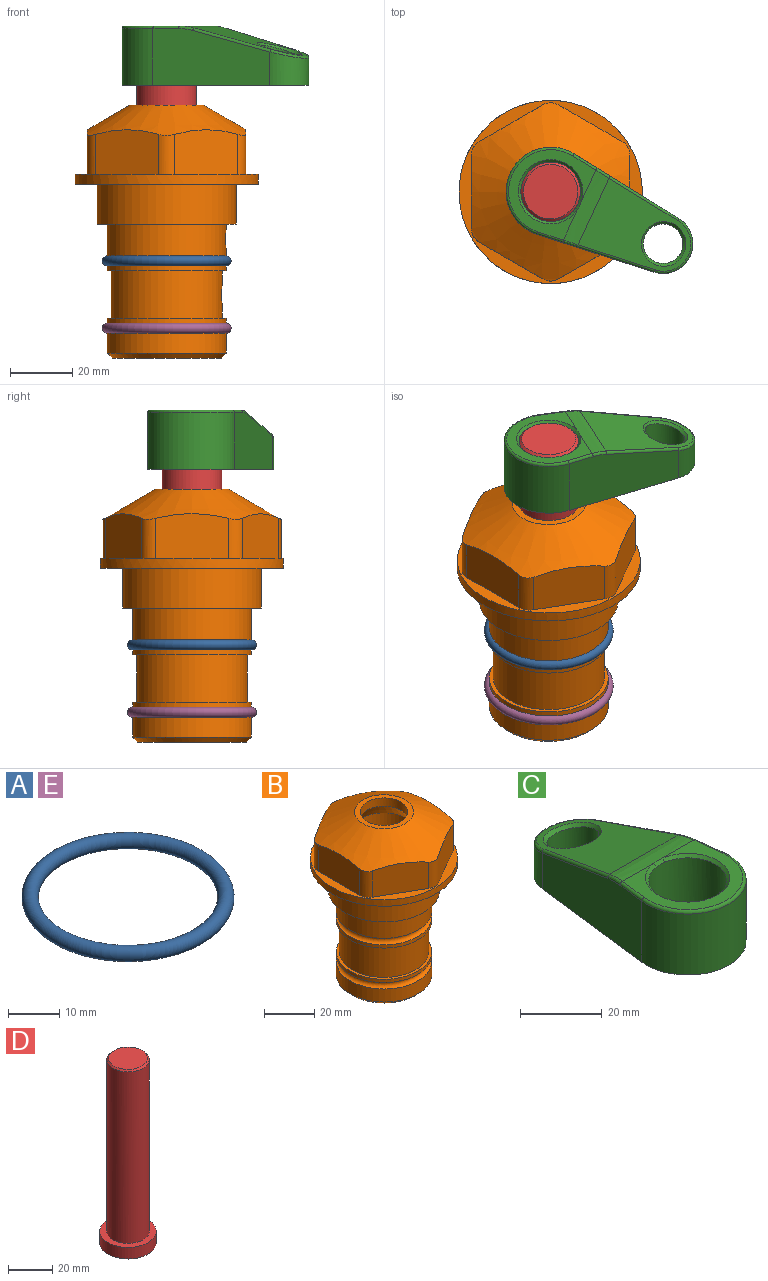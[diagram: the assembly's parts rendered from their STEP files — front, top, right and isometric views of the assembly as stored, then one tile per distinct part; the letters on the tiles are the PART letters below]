
ASSEMBLY  parts=5 mates=4
PART A: 1 faces, bbox 44.7x44.7x3.2 mm
  f0: torus R=19.05mm, axis (0,0,1), area 1193.9mm2
PART B: 36 faces, bbox 58.7x58.7x81 mm
  f0: cylinder r=17.78mm len=35.56mm, axis (0,0,1), area 1670.8mm2, adj f23,f24,f31
  f1: cylinder r=19.05mm len=38.1mm, axis (0,0,1), area 1191.9mm2, adj f26,f27,f30
  f2: plane 58.66x58.66mm, normal (0,0,-1), area 1150.6mm2, adj f3,f28
  f3: cylinder r=29.33mm len=58.66mm, axis (0,0,-1), area 585.1mm2, adj f2,f4
  f4: plane 58.66x58.66mm, normal (0,0,1), area 475.9mm2, adj f3,f5,f6,f7,f8,f9,f10,f11
  f5: plane 20.32x14.34mm, normal (-0.5,0.87,0), area 324.4mm2, adj f4,f15,f16,f17
  f6: plane 20.32x14.34mm, normal (0.5,0.87,0), area 324.4mm2, adj f4,f14,f15,f17
  f7: plane 23.48x14.34mm, normal (1,0,0), area 324.4mm2, adj f4,f13,f14,f17
  f8: plane 20.32x14.34mm, normal (0.5,-0.87,0), area 324.4mm2, adj f4,f12,f13,f17
  f9: plane 20.32x14.34mm, normal (-0.5,-0.87,0), area 324.4mm2, adj f4,f11,f12,f17
  f10: plane 23.48x14.34mm, normal (-1,0,0), area 324.4mm2, adj f4,f11,f16,f17
  f11: cylinder r=5.08mm len=12.85mm, axis (0,0,-1), area 67.2mm2, adj f4,f9,f10,f17
  f12: cylinder r=5.08mm len=12.85mm, axis (0,0,-1), area 67.2mm2, adj f4,f8,f9,f17
  f13: cylinder r=5.08mm len=12.85mm, axis (0,0,-1), area 67.2mm2, adj f4,f7,f8,f17
  f14: cylinder r=5.08mm len=12.85mm, axis (0,0,-1), area 67.2mm2, adj f4,f6,f7,f17
  f15: cylinder r=5.08mm len=12.85mm, axis (0,0,-1), area 67.2mm2, adj f4,f5,f6,f17
  f16: cylinder r=5.08mm len=12.85mm, axis (0,0,-1), area 67.2mm2, adj f4,f5,f10,f17
  f17: cone r=11.73mm half-angle=60deg, axis (0,0,-1), area 2071.8mm2, adj f5,f6,f7,f8,f9,f10,f11,f12
  f18: plane 23.46x23.46mm, normal (0,0,1), area 147.4mm2, adj f17,f35
  f19: plane 34.93x34.93mm, normal (0,0,-1), area 958mm2, adj f29
  f20: cylinder r=19.05mm len=38.1mm, axis (0,0,1), area 760.1mm2, adj f21,f29
  f21: torus R=19.05mm, axis (0,0,1), area 565.3mm2, adj f20,f22
  f22: cylinder r=19.05mm len=38.1mm, axis (0,0,1), area 190mm2, adj f21,f23
  f23: plane 38.1x38.1mm, normal (0,0,1), area 146.9mm2, adj f0,f22
  f24: plane 38.1x38.1mm, normal (0,0,-1), area 146.9mm2, adj f0,f25
  f25: cylinder r=19.05mm len=38.1mm, axis (0,0,1), area 190mm2, adj f24,f26
  f26: torus R=19.05mm, axis (0,0,1), area 565.3mm2, adj f1,f25
  f27: plane 44.45x44.45mm, normal (0,0,-1), area 411.7mm2, adj f1,f28
  f28: cylinder r=22.23mm len=44.45mm, axis (0,0,1), area 1773.5mm2, adj f2,f27
  f29: cone r=19.05mm half-angle=45deg, axis (0,0,1), area 257.5mm2, adj f19,f20
  f30: cylinder r=3.17mm len=6.75mm, axis (-1,0,0), area 128mm2, adj f1,f33
  f31: cylinder r=3.17mm len=6.35mm, axis (-1,0,0), area 102.5mm2, adj f0,f33
  f32: plane 25.4x25.4mm, normal (0,0,1), area 506.7mm2, adj f33
  f33: cylinder r=12.7mm len=66.42mm, axis (0,0,-1), area 5236.2mm2, adj f30,f31,f32,f34
  f34: cone r=9.53mm half-angle=30deg, axis (0,0,-1), area 443.4mm2, adj f33,f35
  f35: cylinder r=9.53mm len=19.05mm, axis (0,0,-1), area 240.9mm2, adj f18,f34
PART C: 31 faces, bbox 31.7x65.5x19.8 mm
  f0: plane 39.12x18.26mm, normal (0.99,0.12,0), area 612.2mm2, adj f1,f4,f7,f11,f13,f15
  f1: cylinder r=9.53mm len=18.91mm, axis (0,0,-1), area 296.1mm2, adj f0,f2,f7,f17
  f2: plane 39.12x18.26mm, normal (-0.99,0.12,0), area 612.2mm2, adj f1,f4,f7,f12,f14,f16
  f3: cylinder r=6.35mm len=12.7mm, axis (0,0,-1), area 362.4mm2, adj f7,f18
  f4: cylinder r=14.29mm len=28.58mm, axis (0,0,-1), area 882.2mm2, adj f0,f2,f7,f10
  f5: cylinder r=9.53mm len=19.05mm, axis (0,0,-1), area 1092.6mm2, adj f7,f19,f20
  f6: plane 26.99x23.69mm, normal (0,0,1), area 216.2mm2, adj f9,f10,f11,f12,f19
  f7: plane 63.5x28.58mm, normal (0,0,-1), area 661.8mm2, adj f0,f1,f2,f3,f4,f5,f22,f23
  f8: plane 33.52x23.6mm, normal (0,0.26,0.97), area 486mm2, adj f9,f15,f16,f17,f18
  f9: cylinder r=19.05mm len=24.72mm, axis (1,0,0), area 120.4mm2, adj f6,f8,f13,f14,f20
  f10: torus R=13.49mm, axis (0,0,1), area 59mm2, adj f4,f6,f11,f12
  f11: cylinder r=0.79mm len=8.67mm, axis (0.12,-0.99,0), area 10.8mm2, adj f0,f6,f10,f13
  f12: cylinder r=0.79mm len=8.67mm, axis (0.12,0.99,0), area 10.8mm2, adj f2,f6,f10,f14
  f13: bspline ~4.95x1.42mm, area 6.1mm2, adj f0,f9,f11,f15
  f14: bspline ~4.95x1.42mm, area 6.1mm2, adj f2,f9,f12,f16
  f15: cylinder r=0.79mm len=25.95mm, axis (0.12,-0.96,0.26), area 32.9mm2, adj f0,f8,f13,f17
  f16: cylinder r=0.79mm len=25.95mm, axis (0.12,0.96,-0.26), area 32.9mm2, adj f2,f8,f14,f17
  f17: bspline ~18.91x8.38mm, area 30mm2, adj f1,f8,f15,f16
  f18: bspline ~14.29x14.29mm, area 48.3mm2, adj f3,f8
  f19: cone r=9.53mm half-angle=45deg, axis (0,0,1), area 66.5mm2, adj f5,f6,f20
  f20: bspline ~3.22x0.96mm, area 3.5mm2, adj f5,f9,f19
  f21: plane 2.75x2.72mm, normal (0,0,-1), area 2.9mm2, adj f23,f25,f28
  f22: plane 23.05x15.88mm, normal (-0.99,-0.12,0), area 323.6mm2, adj f7,f25,f26,f27,f28,f29
  f23: plane 23.05x15.88mm, normal (0.99,-0.12,0), area 323.6mm2, adj f7,f21,f25,f27,f28,f30
  f24: cylinder r=9.53mm len=10.69mm, axis (0,0,-1), area 114.7mm2, adj f7,f27,f29,f30
  f25: cylinder r=12.7mm len=20.59mm, axis (0,0,-1), area 381.1mm2, adj f7,f21,f22,f23,f26,f28
  f26: plane 2.75x2.72mm, normal (0,0,-1), area 2.9mm2, adj f22,f25,f28
  f27: plane 19.72x18.37mm, normal (0,-0.26,-0.97), area 291.8mm2, adj f22,f23,f24,f28,f29,f30
  f28: cylinder r=15.88mm len=19.92mm, axis (1,0,0), area 54.8mm2, adj f21,f22,f23,f25,f26,f27
  f29: cylinder r=1.59mm len=11mm, axis (0,0,-1), area 34.7mm2, adj f7,f22,f24,f27
  f30: cylinder r=1.59mm len=11mm, axis (0,0,-1), area 34.7mm2, adj f7,f23,f24,f27
PART D: 6 faces, bbox 25.4x25.4x101.6 mm
  f0: plane 17.46x17.46mm, normal (0,0,1), area 239.5mm2, adj f5
  f1: plane 25.4x25.4mm, normal (0,0,-1), area 506.7mm2, adj f2
  f2: cylinder r=12.7mm len=25.4mm, axis (0,0,1), area 506.7mm2, adj f1,f3
  f3: plane 25.4x25.4mm, normal (0,0,1), area 221.7mm2, adj f2,f4
  f4: cylinder r=9.53mm len=94.46mm, axis (0,0,1), area 5653mm2, adj f3,f5
  f5: cone r=8.73mm half-angle=45deg, axis (0,0,-1), area 64.4mm2, adj f0,f4
PART E: same geometry as A
PLACE A at identity
PLACE B at identity fixed
PLACE C rot(axis=(0,0,-1),114.8deg) t=(0,0,-12.76)mm
PLACE D rot(axis=(0,0,-1),114.8deg) t=(0,0,-12.76)mm
PLACE E t=(0,0,-21.59)mm
MATE fastened E.f0 <-> B.f0  axis (0,0,1) through (0,0,-46.1)mm
MATE fastened C.f4 <-> D.f2  axis (0,0,1) through (0,0,50.74)mm
MATE cylindrical B.f0 <-> D.f2  axis (0,0,1) through (0,0,-50.86)mm
MATE fastened A.f0 <-> B.f0  axis (0,0,1) through (0,0,-24.51)mm
